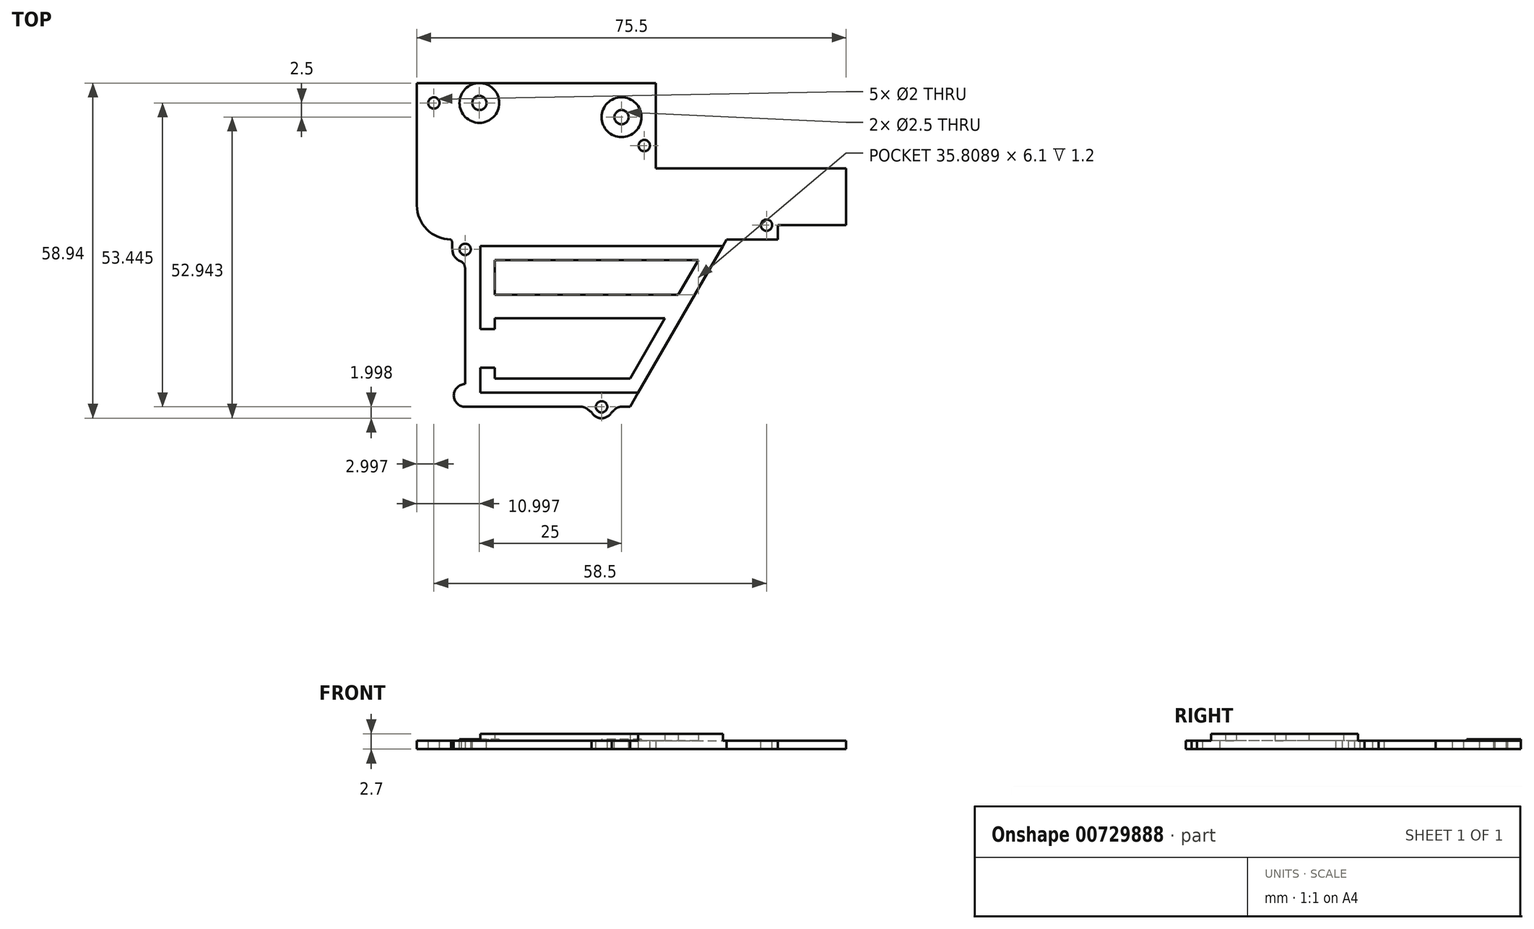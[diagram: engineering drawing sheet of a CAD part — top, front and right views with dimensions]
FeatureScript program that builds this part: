
annotation { "Feature Type Name" : "Feature", "Feature Type Description" : "" }
export const myFeature = defineFeature(function(context is Context, id is Id, definition is map)
    precondition{}
    {
        {
            var Q0;
            Q0=qCreatedBy(makeId("Top.planeOp"),FACE);
            var sketch = newSketch(context, id + "F0", { "sketchPlane" : qUnion([Q0])});
            skLineSegment(sketch, "E0.bottom", {"start": v(10.38, 28.25) * mm, "end": v(43.88, 28.25) * mm});
            skLineSegment(sketch, "E0.top", {"start": v(10.38, 18.25) * mm, "end": v(43.88, 18.25) * mm});
            skLineSegment(sketch, "E0.left", {"start": v(10.38, 28.25) * mm, "end": v(10.38, 18.25) * mm});
            skLineSegment(sketch, "E0.right", {"start": v(43.88, 28.25) * mm, "end": v(43.88, 18.25) * mm});
            skLineSegment(sketch, "E1.bottom", {"start": v(10.38, 18.25) * mm, "end": v(31.88, 18.25) * mm});
            skLineSegment(sketch, "E1.top", {"start": v(10.38, 15.75) * mm, "end": v(31.88, 15.75) * mm});
            skLineSegment(sketch, "E1.left", {"start": v(10.38, 18.25) * mm, "end": v(10.38, 15.75) * mm});
            skLineSegment(sketch, "E1.right", {"start": v(31.88, 18.25) * mm, "end": v(31.88, 15.75) * mm});
            skLineSegment(sketch, "E2.bottom", {"start": v(10.38, 28.25) * mm, "end": v(-31.62, 28.25) * mm});
            skLineSegment(sketch, "E2.top", {"start": v(10.38, 43.25) * mm, "end": v(-31.62, 43.25) * mm});
            skLineSegment(sketch, "E2.left", {"start": v(10.38, 28.25) * mm, "end": v(10.38, 43.25) * mm});
            skLineSegment(sketch, "E2.right", {"start": v(-31.62, 28.25) * mm, "end": v(-31.62, 43.25) * mm});
            skLineSegment(sketch, "E3.bottom", {"start": v(10.38, 15.75) * mm, "end": v(-25.62, 15.75) * mm});
            skLineSegment(sketch, "E3.left", {"start": v(10.38, 15.75) * mm, "end": v(10.38, 28.25) * mm});
            skLineSegment(sketch, "E3.right", {"start": v(-31.62, 21.75) * mm, "end": v(-31.62, 28.25) * mm});
            skLineSegment(sketch, "E4.bottom", {"start": v(-23.12, 15.75) * mm, "end": v(5.88, 15.75) * mm});
            skLineSegment(sketch, "E4.top", {"start": v(-23.12, -13.7) * mm, "end": v(5.88, -13.7) * mm});
            skLineSegment(sketch, "E4.left", {"start": v(-23.12, 15.75) * mm, "end": v(-23.12, -13.7) * mm});
            skLineSegment(sketch, "E4.right", {"start": v(5.88, 15.75) * mm, "end": v(5.88, -13.7) * mm});
            skCircle(sketch, "E5", {"center": v(-23.12, 14) * mm, "radius": 1.25 * mm, "construction": true});
            skArc(sketch, "E6", {"start": v(-23.12, 11.75) * mm, "mid": v(-25.24, 13.25) * mm, "end": v(-24.54, 15.75) * mm});
            skPoint(sketch, "E7.visualSharp", {"position": v(-31.62, 15.75) * mm});
            skArc(sketch, "E7.filletArc", {"start": v(-31.62, 21.75) * mm, "mid": v(-29.87, 17.51) * mm, "end": v(-25.62, 15.75) * mm});
            skFitSpline(sketch, "E8", {"points": [v(-25.62, 15.75) * mm, v(-25.37, 14) * mm], "startDerivative": vector(1.15, -1.43) * mm, "endDerivative": vector(0.25, -1.75) * mm});
            skFitSpline(sketch, "E9", {"points": [v(-23.79, 11.85) * mm, v(-23.12, 10.7) * mm], "startDerivative": vector(2, -1.63) * mm, "endDerivative": vector(0.58, -2) * mm});
            skCircle(sketch, "E10", {"center": v(-28.62, 39.75) * mm, "radius": 1 * mm, "construction": true});
            skCircle(sketch, "E11", {"center": v(-20.62, 39.75) * mm, "radius": 1.25 * mm, "construction": true});
            skCircle(sketch, "E12", {"center": v(-20.62, 39.75) * mm, "radius": 3.5 * mm, "construction": true});
            skCircle(sketch, "E13", {"center": v(4.38, 37.25) * mm, "radius": 1.25 * mm, "construction": true});
            skCircle(sketch, "E14", {"center": v(4.38, 37.25) * mm, "radius": 3.5 * mm, "construction": true});
            skCircle(sketch, "E15", {"center": v(8.38, 32.25) * mm, "radius": 1 * mm, "construction": true});
            skCircle(sketch, "E16", {"center": v(29.88, 18.25) * mm, "radius": 1 * mm, "construction": true});
            skArc(sketch, "E17", {"start": v(-23.12, -9.7) * mm, "mid": v(-25.12, -11.7) * mm, "end": v(-23.12, -13.7) * mm});
            skCircle(sketch, "E18", {"center": v(0.88, -13.7) * mm, "radius": 1 * mm, "construction": true});
            skArc(sketch, "E19", {"start": v(-1.12, -13.7) * mm, "mid": v(0.88, -15.7) * mm, "end": v(2.88, -13.7) * mm});
            skFitSpline(sketch, "E20", {"points": [v(-0.9, -14.6) * mm, v(-2.57, -13.7) * mm], "startDerivative": vector(-1.67, 0.9) * mm, "endDerivative": vector(-2.08, 0) * mm});
            skFitSpline(sketch, "E21", {"points": [v(2.65, -14.62) * mm, v(4.23, -13.7) * mm], "startDerivative": vector(1.58, 0.92) * mm, "endDerivative": vector(2.44, 0) * mm});
            skLineSegment(sketch, "E22", {"start": v(5.88, -13.7) * mm, "end": v(22.88, 15.75) * mm});
            skSolve(sketch);
        }
        {
            var Q0;
            Q0=makeQuery(id+"F0.imprint","IMPRINT",FACE,{"disambiguationData":[TD([[makeQuery(id+"F0.imprint","IMPRINT",EDGE,{"derivedFrom":sQuery(id+"F0.wireOp",EDGE,"E2.bottom")}),-1.0]])]});
            var Q1;
            Q1=makeQuery(id+"F0.imprint","IMPRINT",FACE,{"disambiguationData":[TD([[makeQuery(id+"F0.imprint","IMPRINT",EDGE,{"derivedFrom":sQuery(id+"F0.wireOp",EDGE,"E0.left")}),-1.0]])]});
            var Q2;
            Q2=makeQuery(id+"F0.imprint","IMPRINT",FACE,{"disambiguationData":[TD([[makeQuery(id+"F0.imprint","IMPRINT",EDGE,{"derivedFrom":sQuery(id+"F0.wireOp",EDGE,"E0.bottom")}),-1.0]])]});
            var Q3;
            {var subQ0=sQuery(id+"F0.wireOp",EDGE,"E1.left");Q3=makeQuery(id+"F0.imprint","IMPRINT",FACE,{"disambiguationData":[TD([[makeQuery(id+"F0.imprint","IMPRINT",EDGE,{"derivedFrom":subQ0}),1.0]])]});}
            var Q4;
            {var subQ4=sQuery(id+"F0.wireOp",EDGE,"E4.right");Q4=makeQuery(id+"F0.imprint","IMPRINT",FACE,{"disambiguationData":[TD([[makeQuery(id+"F0.imprint","IMPRINT",EDGE,{"derivedFrom":subQ4}),1.0]])]});}
            var Q5;
            {var subQ14=sQuery(id+"F0.wireOp",EDGE,"E4.right");Q5=makeQuery(id+"F0.imprint","IMPRINT",FACE,{"disambiguationData":[TD([[makeQuery(id+"F0.imprint","IMPRINT",EDGE,{"derivedFrom":subQ14}),-1.0]])]});}
            var Q6;
            {var subQ0=sQuery(id+"F0.wireOp",EDGE,"E8");Q6=makeQuery(id+"F0.imprint","IMPRINT",FACE,{"disambiguationData":[TD([[makeQuery(id+"F0.imprint","IMPRINT",EDGE,{"derivedFrom":subQ0}),1.0]])]});}
            var Q7;
            {var subQ0=sQuery(id+"F0.wireOp",EDGE,"E6");var subQ5=sQuery(id+"F0.wireOp",EDGE,"E3.bottom");var subQ7=makeQuery(id+"F0.imprint","INTERSECT",VERTEX,{"derivedFrom":[subQ5,subQ0]});Q7=makeQuery(id+"F0.imprint","IMPRINT",FACE,{"disambiguationData":[TD([[makeQuery(id+"F0.imprint","IMPRINT",EDGE,{"disambiguationData":[TD([[subQ7,1.0]])],"derivedFrom":subQ5}),1.0]])]});}
            var Q8;
            {var subQ0=sQuery(id+"F0.wireOp",EDGE,"E17");Q8=makeQuery(id+"F0.imprint","IMPRINT",FACE,{"disambiguationData":[TD([[makeQuery(id+"F0.imprint","IMPRINT",EDGE,{"derivedFrom":subQ0}),1.0]])]});}
            var Q9;
            {var subQ0=sQuery(id+"F0.wireOp",EDGE,"E21");Q9=makeQuery(id+"F0.imprint","IMPRINT",FACE,{"disambiguationData":[TD([[makeQuery(id+"F0.imprint","IMPRINT",EDGE,{"derivedFrom":subQ0}),1.0]])]});}
            var Q10;
            {var subQ0=sQuery(id+"F0.wireOp",EDGE,"E19");var subQ1=sQuery(id+"F0.wireOp",EDGE,"E4.top");var subQ2=makeQuery(id+"F0.imprint","INTERSECT",VERTEX,{"disambiguationData":[OD(0.0)],"derivedFrom":[subQ1,subQ0]});Q10=makeQuery(id+"F0.imprint","IMPRINT",FACE,{"disambiguationData":[TD([[makeQuery(id+"F0.imprint","IMPRINT",EDGE,{"disambiguationData":[TD([[subQ2,-1.0]])],"derivedFrom":subQ1}),-1.0]])]});}
            var Q11;
            {var subQ3=sQuery(id+"F0.wireOp",EDGE,"E20");Q11=makeQuery(id+"F0.imprint","IMPRINT",FACE,{"disambiguationData":[TD([[makeQuery(id+"F0.imprint","IMPRINT",EDGE,{"derivedFrom":subQ3}),-1.0]])]});}
            var Q12;
            {var subQ0=sQuery(id+"F0.wireOp",EDGE,"E9");Q12=makeQuery(id+"F0.imprint","IMPRINT",FACE,{"disambiguationData":[TD([[makeQuery(id+"F0.imprint","IMPRINT",EDGE,{"derivedFrom":subQ0}),1.0]])]});}
            extrude(context, id + "F1", {"entities" : qUnion([Q0, Q1, Q2, Q3, Q4, Q5, Q6, Q7, Q8, Q9, Q10, Q11, Q12]), "depth" : 1.5 * mm, "offsetDistance" : 25 * mm});
        }
        {
            var Q0;
            Q0=makeQuery(id+"F1.opExtrude","CAP_FACE",FACE,{"disambiguationData":[OSD([sQuery(id+"F0.wireOp",EDGE,"E0.bottom"),sQuery(id+"F0.wireOp",EDGE,"E0.top"),sQuery(id+"F0.wireOp",EDGE,"E0.right"),sQuery(id+"F0.wireOp",EDGE,"E1.top"),sQuery(id+"F0.wireOp",EDGE,"E1.right"),sQuery(id+"F0.wireOp",EDGE,"E2.top"),sQuery(id+"F0.wireOp",EDGE,"E2.left"),sQuery(id+"F0.wireOp",EDGE,"E2.right"),sQuery(id+"F0.wireOp",EDGE,"E3.right"),sQuery(id+"F0.wireOp",EDGE,"E4.top"),sQuery(id+"F0.wireOp",EDGE,"E4.left"),sQuery(id+"F0.wireOp",EDGE,"E6"),sQuery(id+"F0.wireOp",EDGE,"E7.filletArc"),sQuery(id+"F0.wireOp",EDGE,"E8"),sQuery(id+"F0.wireOp",EDGE,"E9"),sQuery(id+"F0.wireOp",EDGE,"E17"),sQuery(id+"F0.wireOp",EDGE,"E19"),sQuery(id+"F0.wireOp",EDGE,"E20"),sQuery(id+"F0.wireOp",EDGE,"E21"),sQuery(id+"F0.wireOp",EDGE,"E22")])],"isStart":false});
            var sketch = newSketch(context, id + "F2", { "sketchPlane" : qUnion([Q0])});
            skCircle(sketch, "E23", {"center": v(-20.62, 39.75) * mm, "radius": 3.5 * mm});
            skCircle(sketch, "E24", {"center": v(4.38, 37.25) * mm, "radius": 3.5 * mm});
            skSolve(sketch);
        }
        {
            var Q0;
            Q0 = qSketchRegion(id + "F2", true);
            extrude(context, id + "F3", {"entities" : qUnion([Q0]), "operationType" : NewBodyOperationType.ADD, "depth" : .25 * mm, "offsetDistance" : 25 * mm});
        }
        {
            var Q0;
            Q0=makeQuery(id+"F3.opExtrude","CAP_FACE",FACE,{"disambiguationData":[OSD([sQuery(id+"F2.wireOp",EDGE,"E24")])],"isStart":false});
            var sketch = newSketch(context, id + "F4", { "sketchPlane" : qUnion([Q0])});
            skCircle(sketch, "E25", {"center": v(4.38, 37.25) * mm, "radius": 1.25 * mm});
            skCircle(sketch, "E26", {"center": v(-20.62, 39.75) * mm, "radius": 1.25 * mm});
            skSolve(sketch);
        }
        {
            var Q0;
            Q0 = qSketchRegion(id + "F4", true);
            extrude(context, id + "F5", {"entities" : qUnion([Q0]), "operationType" : NewBodyOperationType.REMOVE, "oppositeDirection" : true, "depth" : 5 * mm, "offsetDistance" : 25 * mm});
        }
        {
            var Q0;
            Q0=makeQuery(id+"F1.opExtrude","CAP_FACE",FACE,{"disambiguationData":[OSD([sQuery(id+"F0.wireOp",EDGE,"E0.bottom"),sQuery(id+"F0.wireOp",EDGE,"E0.top"),sQuery(id+"F0.wireOp",EDGE,"E0.right"),sQuery(id+"F0.wireOp",EDGE,"E1.top"),sQuery(id+"F0.wireOp",EDGE,"E1.right"),sQuery(id+"F0.wireOp",EDGE,"E2.top"),sQuery(id+"F0.wireOp",EDGE,"E2.left"),sQuery(id+"F0.wireOp",EDGE,"E2.right"),sQuery(id+"F0.wireOp",EDGE,"E3.right"),sQuery(id+"F0.wireOp",EDGE,"E4.top"),sQuery(id+"F0.wireOp",EDGE,"E4.left"),sQuery(id+"F0.wireOp",EDGE,"E6"),sQuery(id+"F0.wireOp",EDGE,"E7.filletArc"),sQuery(id+"F0.wireOp",EDGE,"E8"),sQuery(id+"F0.wireOp",EDGE,"E9"),sQuery(id+"F0.wireOp",EDGE,"E17"),sQuery(id+"F0.wireOp",EDGE,"E19"),sQuery(id+"F0.wireOp",EDGE,"E20"),sQuery(id+"F0.wireOp",EDGE,"E21"),sQuery(id+"F0.wireOp",EDGE,"E22")])],"isStart":false});
            var sketch = newSketch(context, id + "F6", { "sketchPlane" : qUnion([Q0])});
            skCircle(sketch, "E27", {"center": v(-28.62, 39.75) * mm, "radius": 1 * mm});
            skCircle(sketch, "E28", {"center": v(8.38, 32.25) * mm, "radius": 1 * mm});
            skCircle(sketch, "E29", {"center": v(29.88, 18.25) * mm, "radius": 1 * mm});
            skCircle(sketch, "E30", {"center": v(-23.12, 14) * mm, "radius": 1 * mm});
            skCircle(sketch, "E31", {"center": v(0.88, -13.7) * mm, "radius": 1 * mm});
            skSolve(sketch);
        }
        {
            var Q0;
            Q0 = qSketchRegion(id + "F6", true);
            extrude(context, id + "F7", {"entities" : qUnion([Q0]), "operationType" : NewBodyOperationType.REMOVE, "oppositeDirection" : true, "depth" : 5 * mm, "offsetDistance" : 25 * mm});
        }
        {
            var Q0;
            Q0=makeQuery(id+"F1.opExtrude","CAP_FACE",FACE,{"disambiguationData":[OSD([sQuery(id+"F0.wireOp",EDGE,"E0.bottom"),sQuery(id+"F0.wireOp",EDGE,"E0.top"),sQuery(id+"F0.wireOp",EDGE,"E0.right"),sQuery(id+"F0.wireOp",EDGE,"E1.top"),sQuery(id+"F0.wireOp",EDGE,"E1.right"),sQuery(id+"F0.wireOp",EDGE,"E2.top"),sQuery(id+"F0.wireOp",EDGE,"E2.left"),sQuery(id+"F0.wireOp",EDGE,"E2.right"),sQuery(id+"F0.wireOp",EDGE,"E3.right"),sQuery(id+"F0.wireOp",EDGE,"E4.top"),sQuery(id+"F0.wireOp",EDGE,"E4.left"),sQuery(id+"F0.wireOp",EDGE,"E6"),sQuery(id+"F0.wireOp",EDGE,"E7.filletArc"),sQuery(id+"F0.wireOp",EDGE,"E8"),sQuery(id+"F0.wireOp",EDGE,"E9"),sQuery(id+"F0.wireOp",EDGE,"E17"),sQuery(id+"F0.wireOp",EDGE,"E19"),sQuery(id+"F0.wireOp",EDGE,"E20"),sQuery(id+"F0.wireOp",EDGE,"E21"),sQuery(id+"F0.wireOp",EDGE,"E22")])],"isStart":false});
            var sketch = newSketch(context, id + "F8", { "sketchPlane" : qUnion([Q0])});
            skLineSegment(sketch, "E32", {"start": v(-20.42, -6.8) * mm, "end": v(-20.42, -11.2) * mm});
            skLineSegment(sketch, "E33", {"start": v(-20.42, -11.2) * mm, "end": v(7.32, -11.2) * mm});
            skLineSegment(sketch, "E34", {"start": v(7.32, -11.2) * mm, "end": v(22.22, 14.6) * mm});
            skLineSegment(sketch, "E35", {"start": v(22.22, 14.6) * mm, "end": v(-20.42, 14.6) * mm});
            skLineSegment(sketch, "E36", {"start": v(-20.42, 14.6) * mm, "end": v(-20.42, 0) * mm});
            skLineSegment(sketch, "E37", {"start": v(-20.42, 0) * mm, "end": v(-17.92, 0) * mm});
            skLineSegment(sketch, "E38", {"start": v(-17.92, 0) * mm, "end": v(-17.92, 1.9) * mm});
            skLineSegment(sketch, "E39", {"start": v(-17.92, 1.9) * mm, "end": v(12, 1.9) * mm});
            skLineSegment(sketch, "E40", {"start": v(12, 1.9) * mm, "end": v(5.88, -8.7) * mm});
            skLineSegment(sketch, "E41", {"start": v(5.88, -8.7) * mm, "end": v(-17.92, -8.7) * mm});
            skLineSegment(sketch, "E42", {"start": v(-17.92, -8.7) * mm, "end": v(-17.92, -6.8) * mm});
            skLineSegment(sketch, "E43", {"start": v(-17.92, -6.8) * mm, "end": v(-20.42, -6.8) * mm});
            skLineSegment(sketch, "E44", {"start": v(-17.92, 12.1) * mm, "end": v(-17.92, 6) * mm});
            skLineSegment(sketch, "E45", {"start": v(-17.92, 6) * mm, "end": v(14.36, 6) * mm});
            skLineSegment(sketch, "E46", {"start": v(14.36, 6) * mm, "end": v(17.89, 12.1) * mm});
            skLineSegment(sketch, "E47", {"start": v(17.89, 12.1) * mm, "end": v(-17.92, 12.1) * mm});
            skLineSegment(sketch, "E48", {"start": v(12, 1.9) * mm, "end": v(14.36, 6) * mm, "construction": true});
            skSolve(sketch);
        }
        {
            var Q0;
            Q0 = qSketchRegion(id + "F8", true);
            extrude(context, id + "F9", {"entities" : qUnion([Q0]), "operationType" : NewBodyOperationType.ADD, "depth" : 1.2 * mm, "offsetDistance" : 25 * mm});
        }
    });
